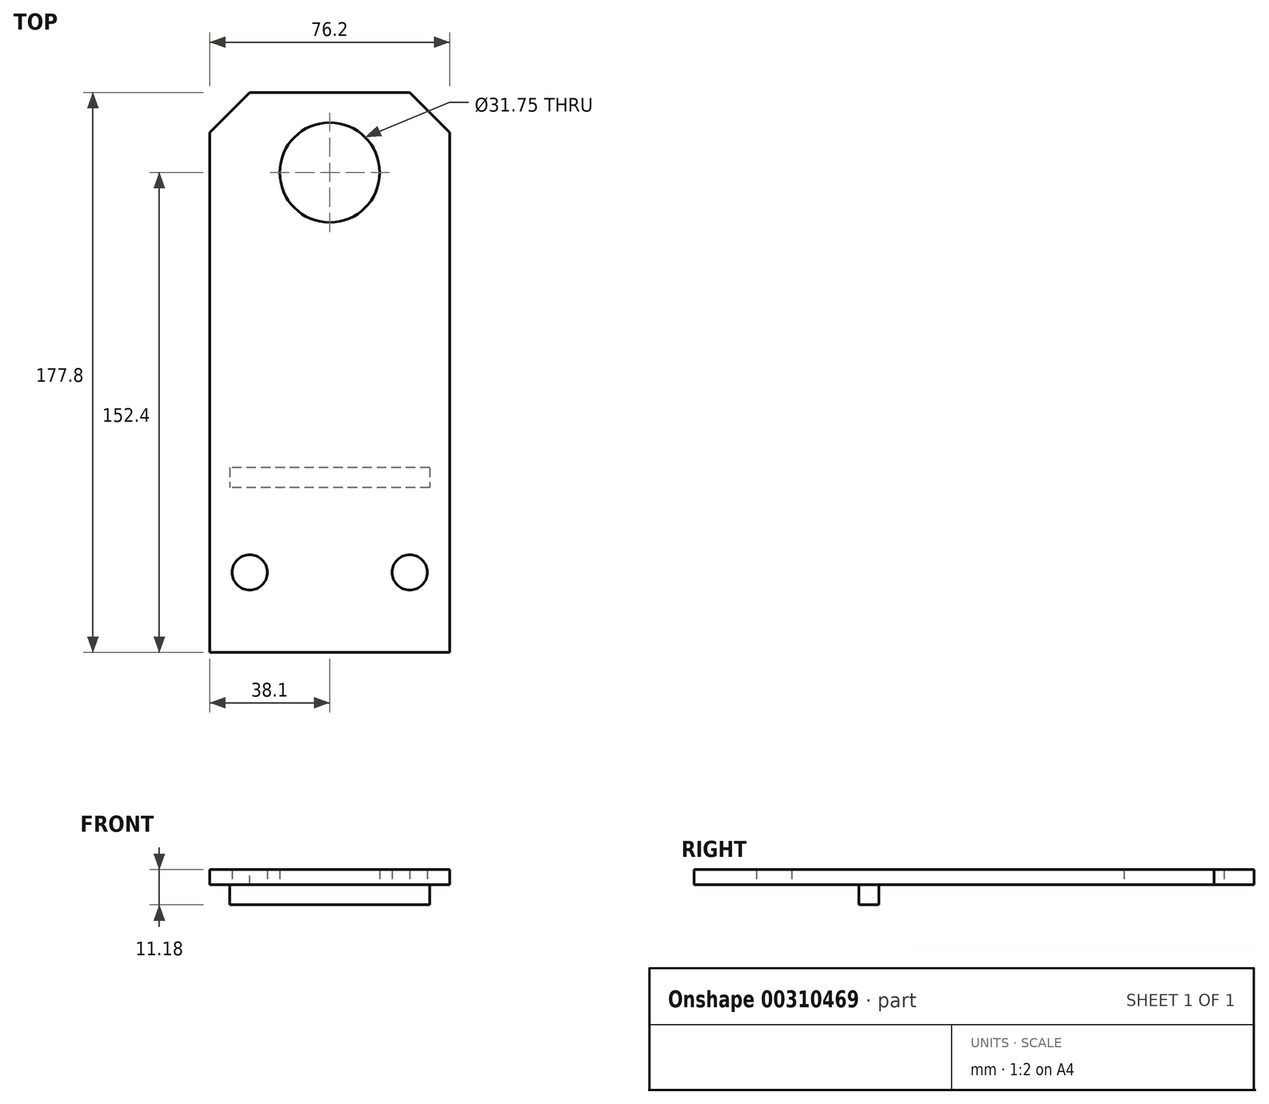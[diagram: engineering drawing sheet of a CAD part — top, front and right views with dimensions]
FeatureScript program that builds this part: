
annotation { "Feature Type Name" : "Feature", "Feature Type Description" : "" }
export const myFeature = defineFeature(function(context is Context, id is Id, definition is map)
    precondition{}
    {
        {
            var Q0;
            Q0=qCreatedBy(makeId("Top.planeOp"),FACE);
            var sketch = newSketch(context, id + "F0", { "sketchPlane" : qUnion([Q0])});
            skCircle(sketch, "E0", {"center": v(0, 0) * mm, "radius": 15.88 * mm});
            skLineSegment(sketch, "E1.left", {"start": v(-38.1, 25.4) * mm, "end": v(-38.1, -152.4) * mm});
            skLineSegment(sketch, "E1.right", {"start": v(38.1, 25.4) * mm, "end": v(38.1, -152.4) * mm});
            skLineSegment(sketch, "E2", {"start": v(-98.95, 0) * mm, "end": v(99.97, 0) * mm, "construction": true});
            skPoint(sketch, "E2.endSnap0", {"position": v(38.1, 0) * mm});
            skLineSegment(sketch, "E3.0", {"start": v(-98.95, -127) * mm, "end": v(99.97, -127) * mm, "construction": true});
            skLineSegment(sketch, "E4.0", {"start": v(-98.95, -152.4) * mm, "end": v(99.97, -152.4) * mm});
            skLineSegment(sketch, "E5.0", {"start": v(-98.95, 25.4) * mm, "end": v(99.97, 25.4) * mm});
            skPoint(sketch, "E6.orphan", {"position": v(-38.1, -25.4) * mm});
            skPoint(sketch, "E7.orphan", {"position": v(38.1, -25.4) * mm});
            skLineSegment(sketch, "E8", {"start": v(0, 103.87) * mm, "end": v(0, -177.44) * mm, "construction": true});
            skLineSegment(sketch, "E9.0", {"start": v(-25.4, 103.87) * mm, "end": v(-25.4, -177.44) * mm, "construction": true});
            skCircle(sketch, "E10", {"center": v(-25.4, -127) * mm, "radius": 5.59 * mm});
            skCircle(sketch, "E11.MirrorC", {"center": v(25.4, -127) * mm, "radius": 5.59 * mm});
            skSolve(sketch);
        }
        {
            var Q0;
            Q0 = qSketchRegion(id + "F0", true);
            extrude(context, id + "F1", {"entities" : qUnion([Q0]), "depth" : 4.83 * mm});
        }
        {
            var Q0;
            Q0=makeQuery(id+"F1.opExtrude","SWEPT_EDGE",EDGE,{"disambiguationData":[OSD([sQuery(id+"F0.wireOp",EDGE,"E1.right"),sQuery(id+"F0.wireOp",EDGE,"E5.0")])]});
            var Q1;
            Q1=makeQuery(id+"F1.opExtrude","SWEPT_EDGE",EDGE,{"disambiguationData":[OSD([sQuery(id+"F0.wireOp",EDGE,"E1.left"),sQuery(id+"F0.wireOp",EDGE,"E5.0")])]});
            chamfer(context, id + "F2", {"entities" : qUnion([Q0, Q1]), "width" : 12.7 * mm, "tangentPropagation" : true});
        }
        {
            var Q0;
            Q0=makeQuery(id+"F1.opExtrude","CAP_FACE",FACE,{"disambiguationData":[OSD([sQuery(id+"F0.wireOp",EDGE,"E0"),sQuery(id+"F0.wireOp",EDGE,"E1.left"),sQuery(id+"F0.wireOp",EDGE,"E1.right"),sQuery(id+"F0.wireOp",EDGE,"E4.0"),sQuery(id+"F0.wireOp",EDGE,"E5.0"),sQuery(id+"F0.wireOp",EDGE,"E10"),sQuery(id+"F0.wireOp",EDGE,"E11.MirrorC")])],"isStart":true});
            var sketch = newSketch(context, id + "F3", { "sketchPlane" : qUnion([Q0])});
            skLineSegment(sketch, "E12", {"start": v(101.78, 0) * mm, "end": v(-97.14, 0) * mm, "construction": true});
            skLineSegment(sketch, "E13", {"start": v(0, 232.58) * mm, "end": v(0, -70.1) * mm, "construction": true});
            skLineSegment(sketch, "E14.0", {"start": v(-31.75, 232.58) * mm, "end": v(-31.75, -70.1) * mm, "construction": true});
            skLineSegment(sketch, "E15.MirrorCS", {"start": v(31.75, 232.58) * mm, "end": v(31.75, -70.1) * mm, "construction": true});
            skLineSegment(sketch, "E16.0", {"start": v(101.78, 93.73) * mm, "end": v(-97.14, 93.73) * mm, "construction": true});
            skLineSegment(sketch, "E17.bottom", {"start": v(31.75, 93.73) * mm, "end": v(-31.75, 93.73) * mm});
            skLineSegment(sketch, "E17.top", {"start": v(31.75, 100.08) * mm, "end": v(-31.75, 100.08) * mm});
            skLineSegment(sketch, "E17.left", {"start": v(31.75, 93.73) * mm, "end": v(31.75, 100.08) * mm});
            skLineSegment(sketch, "E17.right", {"start": v(-31.75, 93.73) * mm, "end": v(-31.75, 100.08) * mm});
            skSolve(sketch);
        }
        {
            var Q0;
            Q0 = qSketchRegion(id + "F3", true);
            extrude(context, id + "F4", {"entities" : qUnion([Q0]), "operationType" : NewBodyOperationType.ADD, "depth" : 6.35 * mm});
        }
    });
